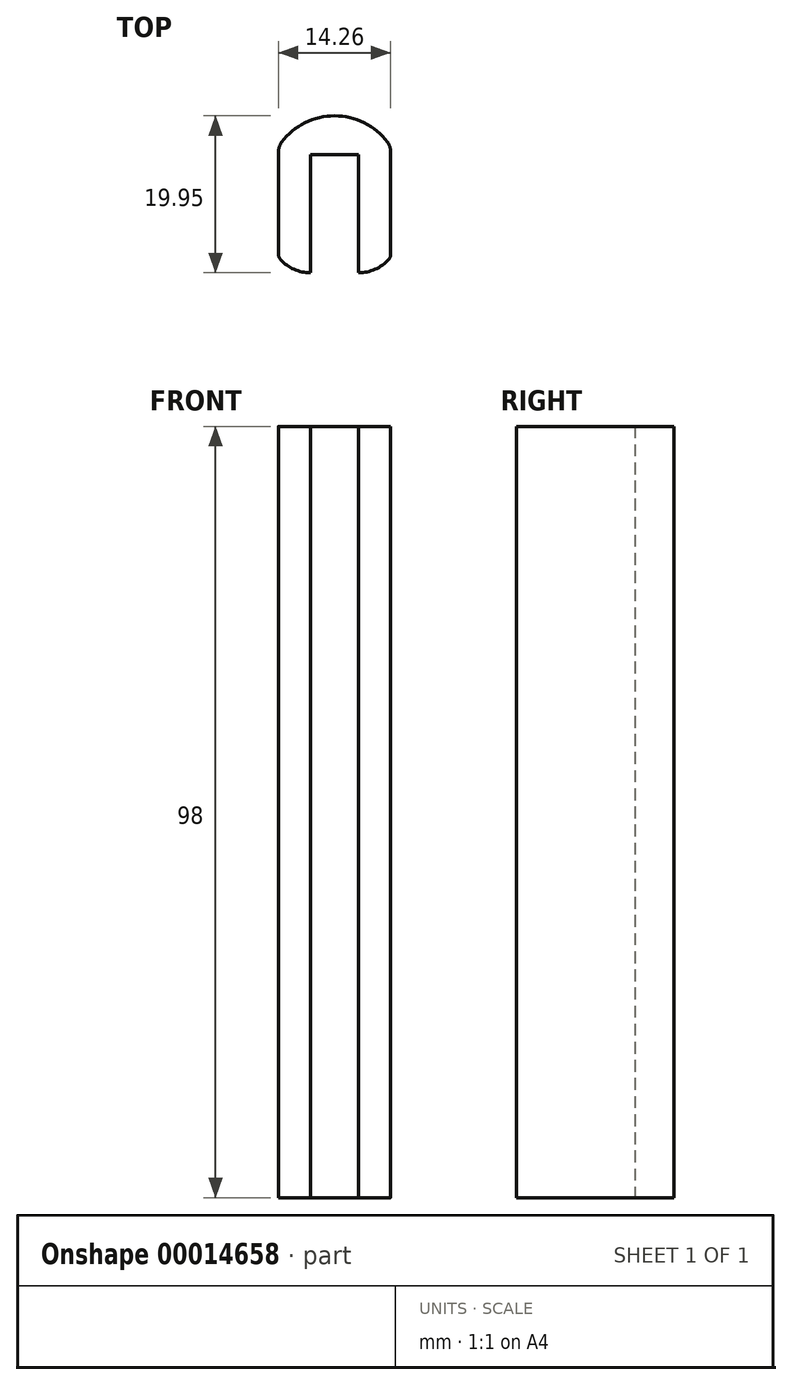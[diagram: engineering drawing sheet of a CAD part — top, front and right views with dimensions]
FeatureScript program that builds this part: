
annotation { "Feature Type Name" : "Feature", "Feature Type Description" : "" }
export const myFeature = defineFeature(function(context is Context, id is Id, definition is map)
    precondition{}
    {
        {
            var Q0;
            Q0=qCreatedBy(makeId("Top.planeOp"),FACE);
            var sketch = newSketch(context, id + "F0", { "sketchPlane" : qUnion([Q0])});
            skLineSegment(sketch, "E0.bottom", {"start": v(-3.06, 0) * mm, "end": v(3.06, 0) * mm});
            skLineSegment(sketch, "E0.left", {"start": v(-3.06, 0) * mm, "end": v(-3.06, -15) * mm});
            skLineSegment(sketch, "E0.right", {"start": v(3.06, 0) * mm, "end": v(3.06, -15) * mm});
            skLineSegment(sketch, "E1.left", {"start": v(-7.13, 0.38) * mm, "end": v(-7.12, -12.64) * mm});
            skLineSegment(sketch, "E1.right", {"start": v(7.12, 0.38) * mm, "end": v(7.13, -12.64) * mm});
            skArc(sketch, "E2", {"start": v(-6.87, -13.3) * mm, "mid": v(-5.14, -14.56) * mm, "end": v(-3.06, -15) * mm});
            skArc(sketch, "E3", {"start": v(3.06, -15) * mm, "mid": v(5.14, -14.56) * mm, "end": v(6.87, -13.3) * mm});
            skArc(sketch, "E4", {"start": v(6.73, 1.58) * mm, "mid": v(0, 4.95) * mm, "end": v(-6.73, 1.58) * mm});
            skPoint(sketch, "E5.visualSharp", {"position": v(7.12, 1) * mm});
            skArc(sketch, "E5.filletArc", {"start": v(7.12, 0.38) * mm, "mid": v(7.02, 1.02) * mm, "end": v(6.73, 1.58) * mm});
            skPoint(sketch, "E6.visualSharp", {"position": v(-7.13, 1) * mm});
            skArc(sketch, "E6.filletArc", {"start": v(-6.73, 1.58) * mm, "mid": v(-7.02, 1.02) * mm, "end": v(-7.13, 0.38) * mm});
            skPoint(sketch, "E7.visualSharp", {"position": v(-7.12, -13) * mm});
            skArc(sketch, "E7.filletArc", {"start": v(-7.12, -12.64) * mm, "mid": v(-7.06, -13) * mm, "end": v(-6.87, -13.3) * mm});
            skPoint(sketch, "E8.visualSharp", {"position": v(7.13, -13) * mm});
            skArc(sketch, "E8.filletArc", {"start": v(6.87, -13.3) * mm, "mid": v(7.06, -13) * mm, "end": v(7.13, -12.64) * mm});
            skSolve(sketch);
        }
        {
            var Q0;
            Q0=makeQuery(id+"F0.imprint","IMPRINT",FACE,{"disambiguationData":[TD([[makeQuery(id+"F0.imprint","IMPRINT",EDGE,{"derivedFrom":sQuery(id+"F0.wireOp",EDGE,"E0.bottom")}),1.0]])]});
            extrude(context, id + "F1", {"entities" : qUnion([Q0]), "depth" : 98 * mm});
        }
    });
